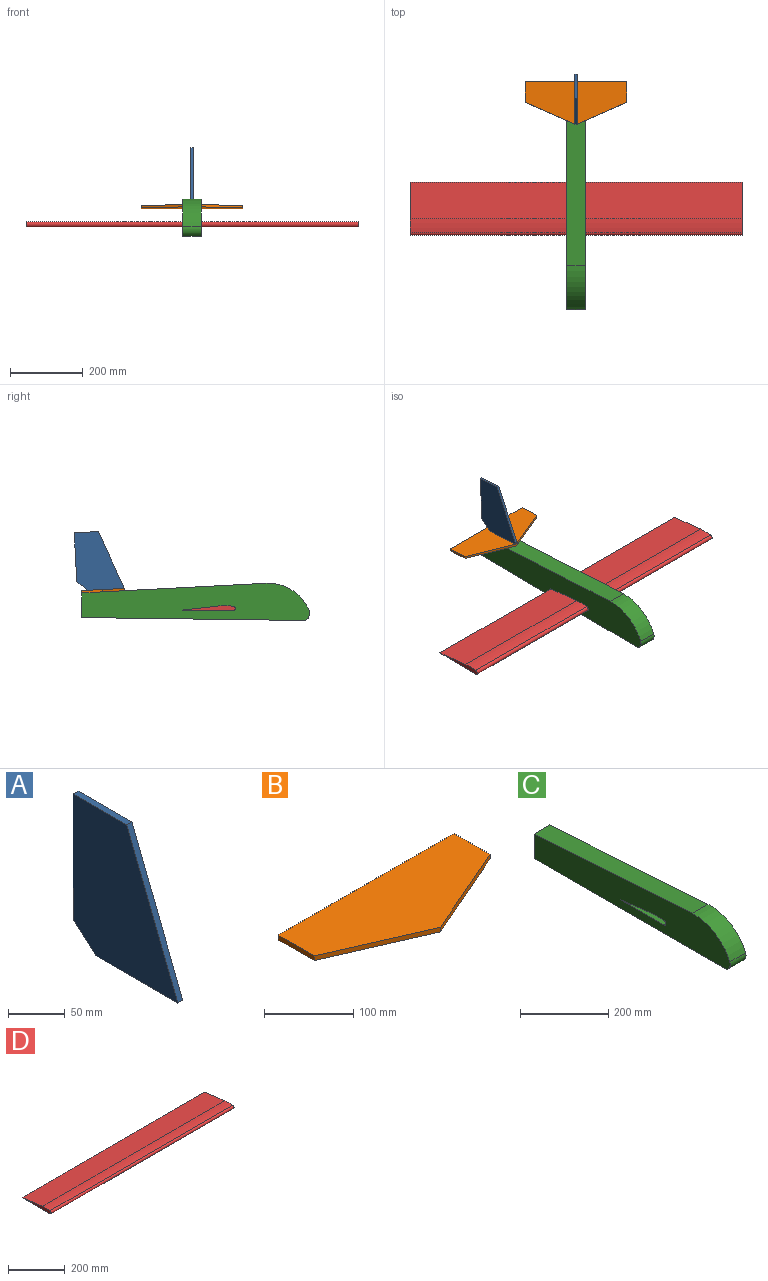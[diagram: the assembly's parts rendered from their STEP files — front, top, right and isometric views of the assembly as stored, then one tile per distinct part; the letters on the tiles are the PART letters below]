
ASSEMBLY  parts=4 mates=3
PART A: 7 faces, bbox 6.4x130x160 mm
  f0: plane 101.6x6.35mm, normal (0,0,-1), area 645.2mm2, adj f1,f4,f5,f6
  f1: plane 28.4x25.4mm, normal (0,0.67,-0.75), area 241.9mm2, adj f0,f2,f5,f6
  f2: plane 134.62x6.35mm, normal (0,1,0), area 854.8mm2, adj f1,f3,f5,f6
  f3: plane 66.5x6.35mm, normal (0,0,1), area 422.3mm2, adj f2,f4,f5,f6
  f4: plane 160.02x63.5mm, normal (0,-0.93,0.37), area 1093.2mm2, adj f0,f3,f5,f6
  f5: plane 160.02x130mm, normal (1,0,0), area 15361mm2, adj f0,f1,f2,f3,f4
  f6: plane 160.02x130mm, normal (-1,0,0), area 15361mm2, adj f0,f1,f2,f3,f4
PART B: 7 faces, bbox 279.4x118.1x6.4 mm
  f0: plane 57.15x6.35mm, normal (-1,0,0), area 362.9mm2, adj f1,f4,f5,f6
  f1: plane 139.7x60.91mm, normal (-0.4,-0.92,0), area 967.7mm2, adj f0,f2,f5,f6
  f2: plane 139.7x60.91mm, normal (0.4,-0.92,0), area 967.7mm2, adj f1,f3,f5,f6
  f3: plane 57.15x6.35mm, normal (1,0,0), area 362.9mm2, adj f2,f4,f5,f6
  f4: plane 279.4x6.35mm, normal (0,1,0), area 1774.2mm2, adj f0,f3,f5,f6
  f5: plane 279.4x118.06mm, normal (0,0,1), area 24476.4mm2, adj f0,f1,f2,f3,f4
  f6: plane 279.4x118.06mm, normal (0,0,-1), area 24476.4mm2, adj f0,f1,f2,f3,f4
PART C: 11 faces, bbox 50.8x628.8x101.2 mm
  f0: plane 67.82x50.8mm, normal (0,1,0), area 3445.2mm2, adj f1,f7,f8,f9
  f1: plane 506.92x50.8mm, normal (0,0.07,1), area 25806.4mm2, adj f0,f2,f8,f9
  f2: cylinder r=121.92mm len=120.36mm, axis (-1,0,0), area 7671.1mm2, adj f1,f8,f9,f10
  f3: plane 139.7x50.8mm, normal (0,0,1), area 7096.8mm2, adj f4,f6,f8,f9
  f4: cylinder r=6.35mm len=50.8mm, axis (-1,0,0), area 1013.4mm2, adj f3,f5,f8,f9
  f5: cylinder r=185.15mm len=50.8mm, axis (-1,0,0), area 1979.6mm2, adj f4,f6,f8,f9
  f6: plane 100.8x50.8mm, normal (0,-0.12,-0.99), area 5161.3mm2, adj f3,f5,f8,f9
  f7: plane 609.71x50.8mm, normal (0,0,-1), area 30973.5mm2, adj f0,f8,f9,f10
  f8: plane 628.76x101.16mm, normal (1,0,0), area 51338.2mm2, adj f0,f1,f2,f3,f4,f5,f6,f7
  f9: plane 628.76x101.16mm, normal (-1,0,0), area 51338.2mm2, adj f0,f1,f2,f3,f4,f5,f6,f7
  f10: cylinder r=19.05mm len=50.8mm, axis (-1,0,0), area 1904.7mm2, adj f2,f7,f8,f9
PART D: 6 faces, bbox 914.4x146.1x13.7 mm
  f0: cylinder r=6.35mm len=914.4mm, axis (-1,0,0), area 18241.5mm2, adj f1,f3,f4,f5
  f1: plane 914.4x139.7mm, normal (0,0,-1), area 127741.7mm2, adj f0,f2,f4,f5
  f2: plane 914.4x100.8mm, normal (0,0.12,0.99), area 92903mm2, adj f1,f3,f4,f5
  f3: cylinder r=185.15mm len=914.4mm, axis (-1,0,0), area 35633mm2, adj f0,f2,f4,f5
  f4: plane 146.05x13.72mm, normal (1,0,0), area 1224mm2, adj f0,f1,f2,f3
  f5: plane 146.05x13.72mm, normal (-1,0,0), area 1224mm2, adj f0,f1,f2,f3
PLACE A rot(axis=(-1,0,0),3deg) t=(-79.73,571.7,-71.76)mm
PLACE B rot(axis=(-1,0,0),3deg) t=(-79.73,591.3,-75.96)mm
PLACE C rot(axis=(1,0,0),0.7deg) t=(-79.73,353.45,-151.72)mm
PLACE D rot(axis=(1,0,0),0.7deg) t=(-79.73,239.44,-129.1)mm
MATE fastened D.f2 <-> C.f6  axis (0,0.11,0.99) through (-79.73,239.27,-116.4)mm
MATE fastened B.f6 <-> C.f1  axis (0,-0.05,-1) through (-79.73,616.5,-80.46)mm
MATE fastened A.f0 <-> B.f5  axis (0,-0.05,-1) through (-79.73,498.93,-67.97)mm
